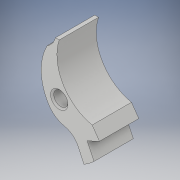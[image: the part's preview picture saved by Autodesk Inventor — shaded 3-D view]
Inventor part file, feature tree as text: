
AUTODESK INVENTOR PART (.ipt)
format: ipt  version: 2018.3 (Build 223284000, 284)  size: 147,456 bytes
history: native  units: in
note: dims shown in document units (in); Inventor stores cm internally (conversion verified against a paired STEP export)
features: extrude x1, chamfer x1, sketch x1
ambient origin geometry x8: Origin, YZ Plane, XZ Plane, XY Plane, X Axis, Y Axis, Z Axis, Center Point
bodies: Solid1 (feature_tree)
feature tree (3):
  extrude  "Extrusion1"  Depth=0.309in
  chamfer  "Chamfer1"  Distance=0.346in
  sketch  "Sketch1"  dims[d0=0.111in d1=0.294in d2=0.346in d3=0.3779in d5=0.186in d6=0.1725in d7=0.249in d8=0.395in d10=0.126in d12=0.03in d13=0.15in d14=0.0115in d15=0.022in d16=0.19in d19=0.284in d20=0.4045in d21=0.4395in d22=0.14in d23=0.03in d24=0.394in d25=0.309in d26=0.0in d27=0.0125in d28=0.125in d29=45.0deg]
